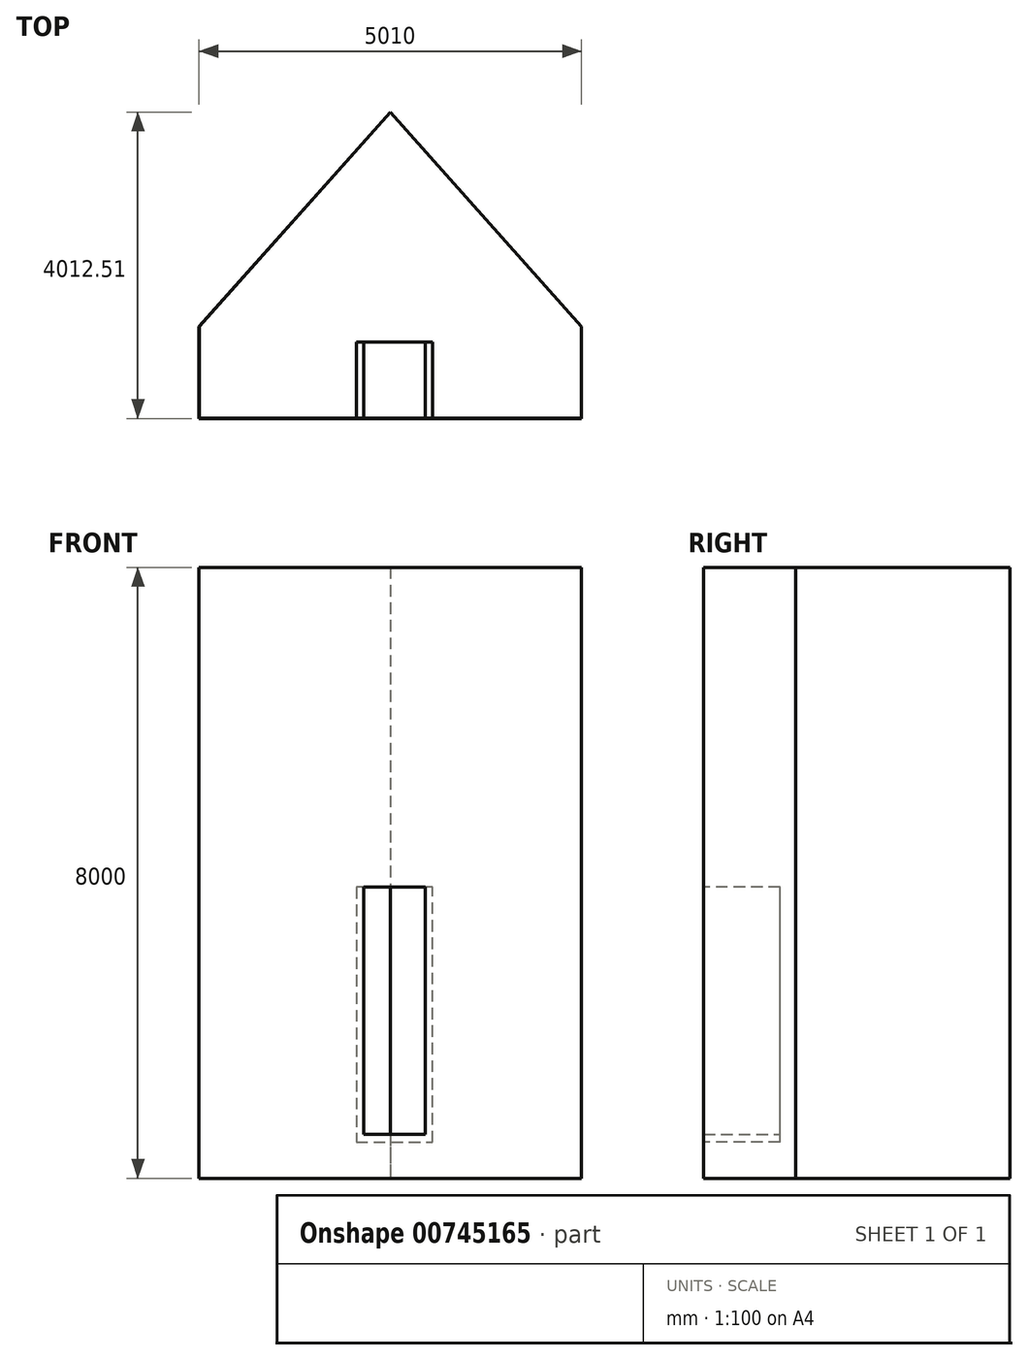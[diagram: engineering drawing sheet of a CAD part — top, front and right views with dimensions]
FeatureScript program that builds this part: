
annotation { "Feature Type Name" : "Feature", "Feature Type Description" : "" }
export const myFeature = defineFeature(function(context is Context, id is Id, definition is map)
    precondition{}
    {
        {
            var Q0;
            Q0=qCreatedBy(makeId("Top.planeOp"),FACE);
            var sketch = newSketch(context, id + "F0", { "sketchPlane" : qUnion([Q0])});
            skLineSegment(sketch, "E0.bottom", {"start": v(-2500, 0) * mm, "end": v(2500, 0) * mm});
            skLineSegment(sketch, "E0.left", {"start": v(-2500, 0) * mm, "end": v(-2500, 1200) * mm});
            skLineSegment(sketch, "E0.right", {"start": v(2500, 0) * mm, "end": v(2500, 1200) * mm});
            skLineSegment(sketch, "E1", {"start": v(-2500, 1200) * mm, "end": v(0, 4000) * mm});
            skLineSegment(sketch, "E2", {"start": v(0, 4000) * mm, "end": v(2500, 1200) * mm});
            skLineSegment(sketch, "E3.0", {"start": v(0, 4007.5) * mm, "end": v(2505, 1201.9) * mm});
            skLineSegment(sketch, "E3.1", {"start": v(2505, -5) * mm, "end": v(2505, 1201.9) * mm});
            skLineSegment(sketch, "E3.2", {"start": v(-2505, 1201.9) * mm, "end": v(0, 4007.5) * mm});
            skLineSegment(sketch, "E3.3", {"start": v(-2505, -5) * mm, "end": v(-2505, 1201.9) * mm});
            skLineSegment(sketch, "E3.4", {"start": v(-2505, -5) * mm, "end": v(2505, -5) * mm});
            skSolve(sketch);
        }
        {
            var Q0;
            Q0=makeQuery(id+"F0.imprint","IMPRINT",FACE,{"disambiguationData":[TD([[makeQuery(id+"F0.imprint","IMPRINT",EDGE,{"derivedFrom":sQuery(id+"F0.wireOp",EDGE,"E0.bottom")}),1.0]])]});
            var Q1;
            Q1=makeQuery(id+"F0.imprint","IMPRINT",FACE,{"disambiguationData":[TD([[makeQuery(id+"F0.imprint","IMPRINT",EDGE,{"derivedFrom":sQuery(id+"F0.wireOp",EDGE,"E0.bottom")}),-1.0]])]});
            extrude(context, id + "F1", {"entities" : qUnion([Q0, Q1]), "depth" : 8000 * mm, "offsetDistance" : 25 * mm});
        }
        {
            var Q0;
            Q0=makeQuery(id+"F1.opExtrude","CAP_FACE",FACE,{"disambiguationData":[OSD([sQuery(id+"F0.wireOp",EDGE,"E3.0"),sQuery(id+"F0.wireOp",EDGE,"E3.1"),sQuery(id+"F0.wireOp",EDGE,"E3.2"),sQuery(id+"F0.wireOp",EDGE,"E3.3"),sQuery(id+"F0.wireOp",EDGE,"E3.4")])],"isStart":false});
            shell(context, id + "F2", {"entities" : qUnion([Q0]), "thickness" : 2.5 * mm});
        }
        {
            var Q0;
            Q0=makeQuery(id+"F2.opShell","OFFSET_FACE",FACE,{"disambiguationData":[OSD([sQuery(id+"F0.wireOp",EDGE,"E3.4")])]});
            var sketch = newSketch(context, id + "F3", { "sketchPlane" : qUnion([Q0])});
            skLineSegment(sketch, "E4.bottom", {"start": v(345.83, 572.63) * mm, "end": v(-456.08, 572.63) * mm});
            skLineSegment(sketch, "E4.top", {"start": v(345.83, 3812.76) * mm, "end": v(-456.08, 3812.76) * mm});
            skLineSegment(sketch, "E4.left", {"start": v(345.83, 572.63) * mm, "end": v(345.83, 3812.76) * mm});
            skLineSegment(sketch, "E4.right", {"start": v(-456.08, 572.63) * mm, "end": v(-456.08, 3812.76) * mm});
            skSolve(sketch);
        }
        {
            var Q0;
            Q0 = qSketchRegion(id + "F3", true);
            extrude(context, id + "F4", {"entities" : qUnion([Q0]), "operationType" : NewBodyOperationType.REMOVE, "oppositeDirection" : true, "depth" : 25 * mm, "offsetDistance" : 25 * mm});
        }
        {
            var Q0;
            Q0=makeQuery(id+"F2.opShell","OFFSET_FACE",FACE,{"disambiguationData":[OSD([sQuery(id+"F0.wireOp",EDGE,"E3.4")])]});
            var sketch = newSketch(context, id + "F5", { "sketchPlane" : qUnion([Q0])});
            skLineSegment(sketch, "E5.bottom", {"start": v(345.83, 3812.76) * mm, "end": v(445.83, 3812.76) * mm});
            skLineSegment(sketch, "E5.left", {"start": v(345.83, 3812.76) * mm, "end": v(345.83, 572.63) * mm});
            skLineSegment(sketch, "E5.right", {"start": v(445.83, 3812.76) * mm, "end": v(445.83, 572.63) * mm});
            skLineSegment(sketch, "E6.bottom", {"start": v(345.83, 572.63) * mm, "end": v(-456.08, 572.63) * mm});
            skLineSegment(sketch, "E6.top", {"start": v(445.83, 472.63) * mm, "end": v(-556.08, 472.63) * mm});
            skLineSegment(sketch, "E6.left", {"start": v(445.83, 572.63) * mm, "end": v(445.83, 472.63) * mm});
            skLineSegment(sketch, "E6.right", {"start": v(-556.08, 572.63) * mm, "end": v(-556.08, 472.63) * mm});
            skLineSegment(sketch, "E7.top", {"start": v(-556.08, 3812.76) * mm, "end": v(-456.08, 3812.76) * mm});
            skLineSegment(sketch, "E7.left", {"start": v(-556.08, 572.63) * mm, "end": v(-556.08, 3812.76) * mm});
            skLineSegment(sketch, "E7.right", {"start": v(-456.08, 572.63) * mm, "end": v(-456.08, 3812.76) * mm});
            skSolve(sketch);
        }
        {
            var Q0;
            Q0 = qSketchRegion(id + "F5", true);
            extrude(context, id + "F6", {"entities" : qUnion([Q0]), "operationType" : NewBodyOperationType.ADD, "depth" : 1000 * mm, "offsetDistance" : 25 * mm});
        }
    });
